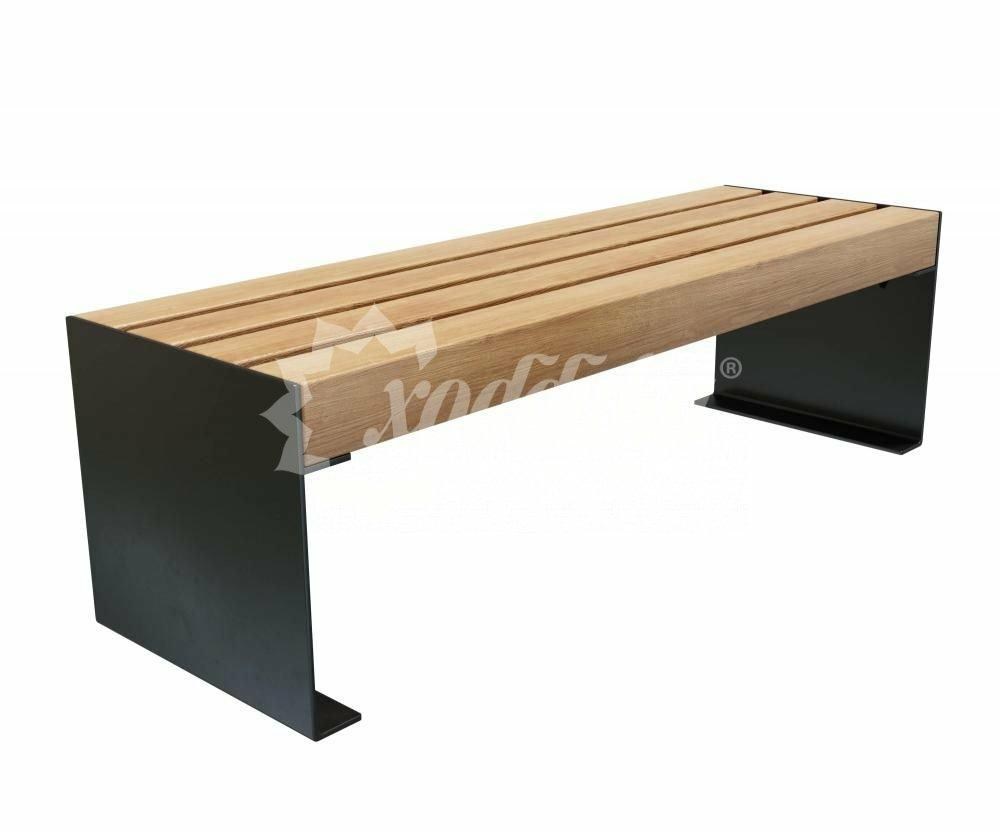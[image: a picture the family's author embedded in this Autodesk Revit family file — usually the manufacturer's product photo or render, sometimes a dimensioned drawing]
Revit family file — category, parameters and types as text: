
# Revit family: Скамейка стальная «Фелисити» без спинки Арт 14545
name_source: partatom
category: Антураж
revit_build: Autodesk Revit 2018 (Build: 20180423_1000(x64)
units: mm (PartAtom-declared; Revit-internal decimal feet)

## family parameters
Всегда вертикально = Да
Источник визуального образа = Геометрия семейства
На основе рабочей плоскости = Нет
Общий = Нет
При загрузке вырезать с полостями = Нет
Точка расчета площади = Нет

## types (3) — shared parameters
URL = https://hobbyka.ru
Артикул товара = Арт 14545
Высота = 450 мм
Группа модели = Садовые скамейки
Изготовитель = ООО «Хоббика»
Изображение типоразмера = Скамейка стальная «Фелисити» без спинки Арт 14545.jpg
Материал изделия = Сталь, дерево
Цвет лавки = Дерево
Цвет опор = Сталь
Ширина = 430 мм

## per-type parameters (varying)
| type | Версия 1,5 м | Версия 1,8 м | Версия 2,0 м | Длина | Описание |
| Версия 1,5 м | Да | Нет | Нет | 1500 мм | Скамейка стальная «Фелисити» без спинки. Версия 1,5 м |
| Версия 1,8 м | Нет | Да | Нет | 1800 мм | Скамейка стальная «Фелисити» без спинки. Версия 1,8 м |
| Версия 2,0 м | Нет | Нет | Да | 2000 мм | Скамейка стальная «Фелисити» без спинки. Версия 2,0 м |
